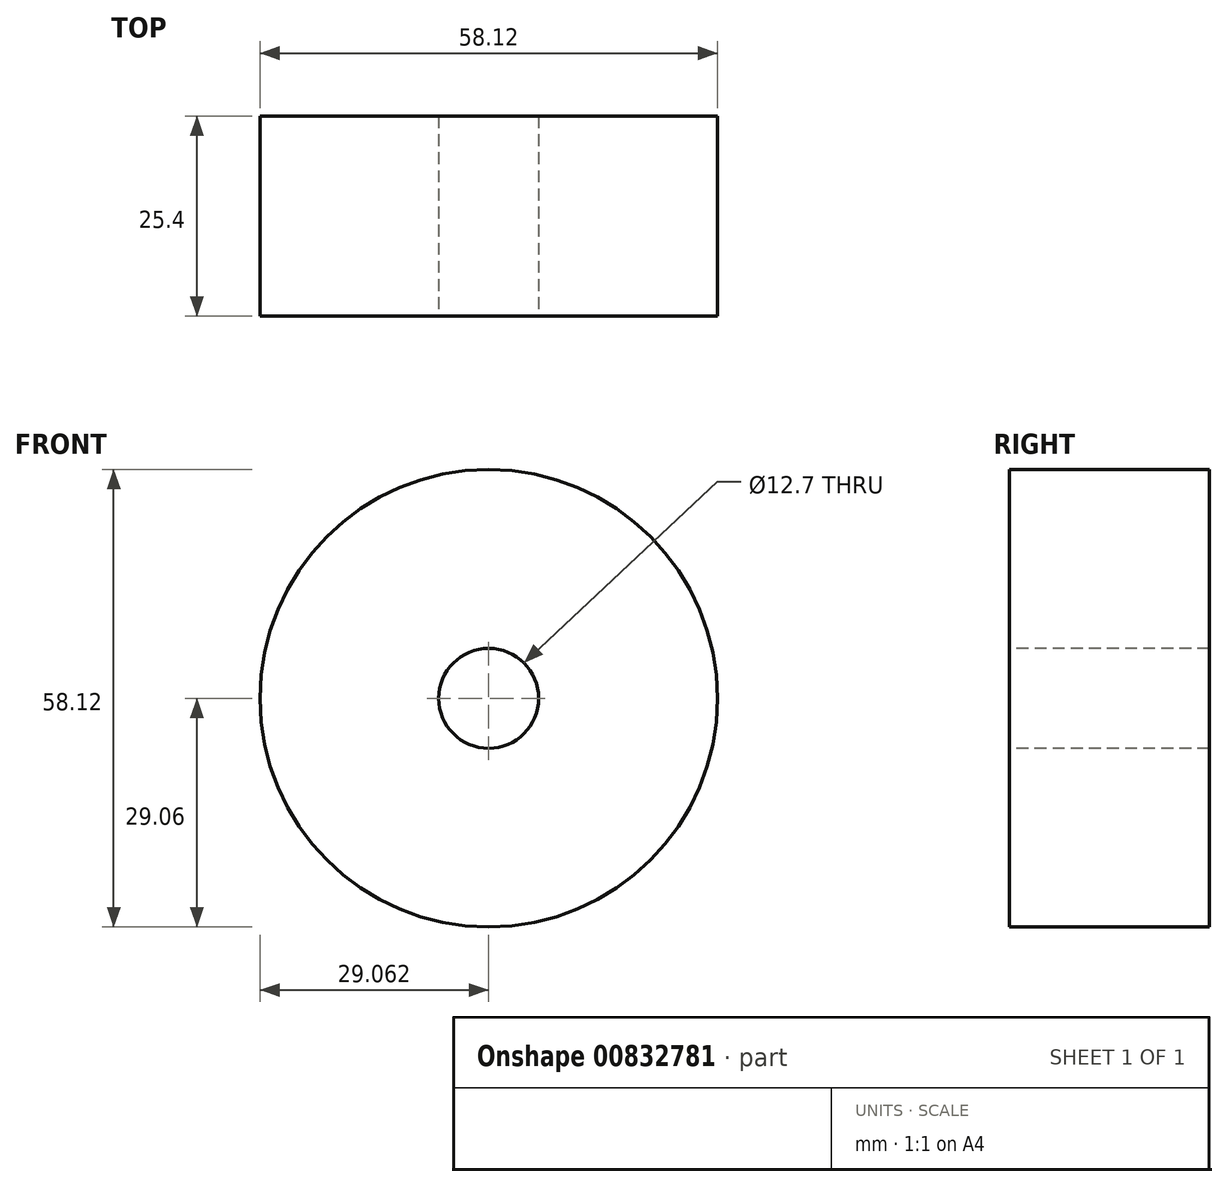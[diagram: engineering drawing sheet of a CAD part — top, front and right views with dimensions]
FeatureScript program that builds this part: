
annotation { "Feature Type Name" : "Feature", "Feature Type Description" : "" }
export const myFeature = defineFeature(function(context is Context, id is Id, definition is map)
    precondition{}
    {
        {
            var Q0;
            Q0=qCreatedBy(makeId("Front.planeOp"),FACE);
            var sketch = newSketch(context, id + "F0", { "sketchPlane" : qUnion([Q0])});
            skCircle(sketch, "E0", {"center": v(-53.12, 0) * mm, "radius": 29.06 * mm});
            skSolve(sketch);
        }
        {
            var Q0;
            Q0 = qSketchRegion(id + "F0", true);
            extrude(context, id + "F1", {"entities" : qUnion([Q0]), "depth" : 25.4 * mm, "offsetDistance" : 25.4 * mm});
        }
        {
            var Q0;
            Q0=makeQuery(id+"F1.opExtrude","CAP_FACE",FACE,{"disambiguationData":[OSD([sQuery(id+"F0.wireOp",EDGE,"E0")])],"isStart":false});
            var sketch = newSketch(context, id + "F2", { "sketchPlane" : qUnion([Q0])});
            skCircle(sketch, "E1", {"center": v(-53.12, 0) * mm, "radius": 6.35 * mm});
            skSolve(sketch);
        }
        {
            var Q0;
            Q0 = qSketchRegion(id + "F2", true);
            extrude(context, id + "F3", {"entities" : qUnion([Q0]), "operationType" : NewBodyOperationType.REMOVE, "endBound" : BoundingType.UP_TO_NEXT, "oppositeDirection" : true, "depth" : 25.4 * mm, "offsetDistance" : 25.4 * mm});
        }
    });
